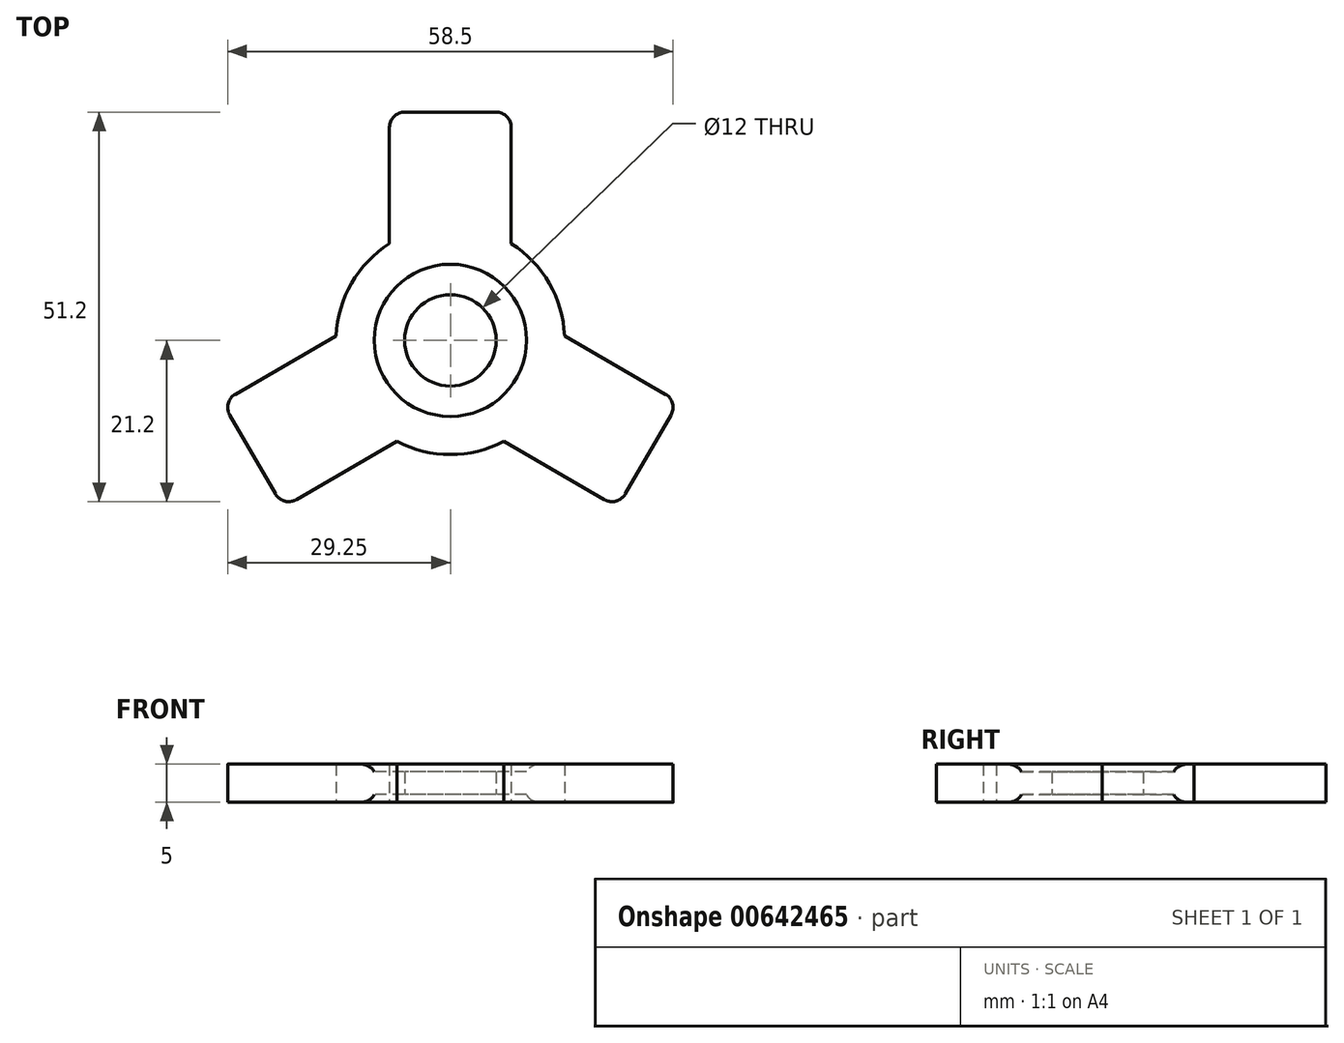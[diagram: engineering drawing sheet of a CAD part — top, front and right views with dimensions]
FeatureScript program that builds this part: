
annotation { "Feature Type Name" : "Feature", "Feature Type Description" : "" }
export const myFeature = defineFeature(function(context is Context, id is Id, definition is map)
    precondition{}
    {
        {
            var Q0;
            Q0=qCreatedBy(makeId("Top.planeOp"),FACE);
            var sketch = newSketch(context, id + "F0", { "sketchPlane" : qUnion([Q0])});
            skCircle(sketch, "E0", {"center": v(0, 0) * mm, "radius": 6 * mm});
            skLineSegment(sketch, "E1", {"start": v(29.98, -8.07) * mm, "end": v(25.98, -15) * mm});
            skLineSegment(sketch, "E2", {"start": v(29.98, -8.07) * mm, "end": v(14.99, 0.58) * mm});
            skLineSegment(sketch, "E3", {"start": v(25.98, -15) * mm, "end": v(21.98, -21.93) * mm});
            skLineSegment(sketch, "E4", {"start": v(21.98, -21.93) * mm, "end": v(6.99, -13.27) * mm});
            skLineSegment(sketch, "E5", {"start": v(-14.99, 0.58) * mm, "end": v(-27.43, -6.6) * mm});
            skLineSegment(sketch, "E6", {"start": v(-6.99, -13.27) * mm, "end": v(-21.98, -21.93) * mm});
            skLineSegment(sketch, "E7", {"start": v(-21.98, -21.93) * mm, "end": v(-29.98, -8.07) * mm});
            skLineSegment(sketch, "E8", {"start": v(-27.43, -6.6) * mm, "end": v(-29.98, -8.07) * mm});
            skLineSegment(sketch, "E9", {"start": v(8, 12.69) * mm, "end": v(8, 30) * mm});
            skLineSegment(sketch, "E10", {"start": v(8, 30) * mm, "end": v(-8, 30) * mm});
            skLineSegment(sketch, "E11", {"start": v(-8, 12.69) * mm, "end": v(-8, 30) * mm});
            skArc(sketch, "E12", {"start": v(-8, 12.69) * mm, "mid": v(-13, 7.5) * mm, "end": v(-14.99, 0.58) * mm});
            skArc(sketch, "E13.trimOffspring", {"start": v(-6.99, -13.27) * mm, "mid": v(0, -15) * mm, "end": v(6.99, -13.27) * mm});
            skArc(sketch, "E14.trimOffspring", {"start": v(14.99, 0.58) * mm, "mid": v(13, 7.5) * mm, "end": v(8, 12.69) * mm});
            skCircle(sketch, "E15", {"center": v(0, 0) * mm, "radius": 10 * mm});
            skSolve(sketch);
        }
        {
            var Q0;
            Q0 = qSketchRegion(id + "F0", true);
            extrude(context, id + "F1", {"entities" : qUnion([Q0]), "endBound" : BoundingType.SYMMETRIC, "depth" : 5 * mm, "offsetDistance" : 25 * mm});
        }
        {
            var Q0;
            Q0=makeQuery(id+"F0.imprint","IMPRINT",FACE,{"disambiguationData":[TD([[makeQuery(id+"F0.imprint","IMPRINT",EDGE,{"derivedFrom":sQuery(id+"F0.wireOp",EDGE,"E0")}),-1.0]])]});
            extrude(context, id + "F2", {"entities" : qUnion([Q0]), "operationType" : NewBodyOperationType.ADD, "endBound" : BoundingType.SYMMETRIC, "depth" : 3 * mm, "offsetDistance" : 25 * mm});
        }
        {
            var Q0;
            Q0=makeQuery(id+"F1.opExtrude","SWEPT_EDGE",EDGE,{"disambiguationData":[OSD([sQuery(id+"F0.wireOp",EDGE,"E7"),sQuery(id+"F0.wireOp",EDGE,"E8")])]});
            var Q1;
            Q1=makeQuery(id+"F1.opExtrude","SWEPT_EDGE",EDGE,{"disambiguationData":[OSD([sQuery(id+"F0.wireOp",EDGE,"E6"),sQuery(id+"F0.wireOp",EDGE,"E7")])]});
            var Q2;
            Q2=makeQuery(id+"F1.opExtrude","SWEPT_EDGE",EDGE,{"disambiguationData":[OSD([sQuery(id+"F0.wireOp",EDGE,"E3"),sQuery(id+"F0.wireOp",EDGE,"E4")])]});
            var Q3;
            Q3=makeQuery(id+"F1.opExtrude","SWEPT_EDGE",EDGE,{"disambiguationData":[OSD([sQuery(id+"F0.wireOp",EDGE,"E1"),sQuery(id+"F0.wireOp",EDGE,"E2")])]});
            var Q4;
            Q4=makeQuery(id+"F1.opExtrude","SWEPT_EDGE",EDGE,{"disambiguationData":[OSD([sQuery(id+"F0.wireOp",EDGE,"E9"),sQuery(id+"F0.wireOp",EDGE,"E10")])]});
            var Q5;
            Q5=makeQuery(id+"F1.opExtrude","SWEPT_EDGE",EDGE,{"disambiguationData":[OSD([sQuery(id+"F0.wireOp",EDGE,"E10"),sQuery(id+"F0.wireOp",EDGE,"E11")])]});
            var Q6;
            Q6=makeQuery(id+"F1.opExtrude","CAP_EDGE",EDGE,{"disambiguationData":[OSD([sQuery(id+"F0.wireOp",EDGE,"E15")])],"isStart":false});
            var Q7;
            Q7=makeQuery(id+"F1.opExtrude","CAP_EDGE",EDGE,{"disambiguationData":[OSD([sQuery(id+"F0.wireOp",EDGE,"E15")])],"isStart":true});
            fillet(context, id + "F3", {"entities" : qUnion([Q0, Q1, Q2, Q3, Q4, Q5, Q6, Q7]), "radius" : 2 * mm, "tangentPropagation" : true, "allowEdgeOverflow" : false});
        }
    });
